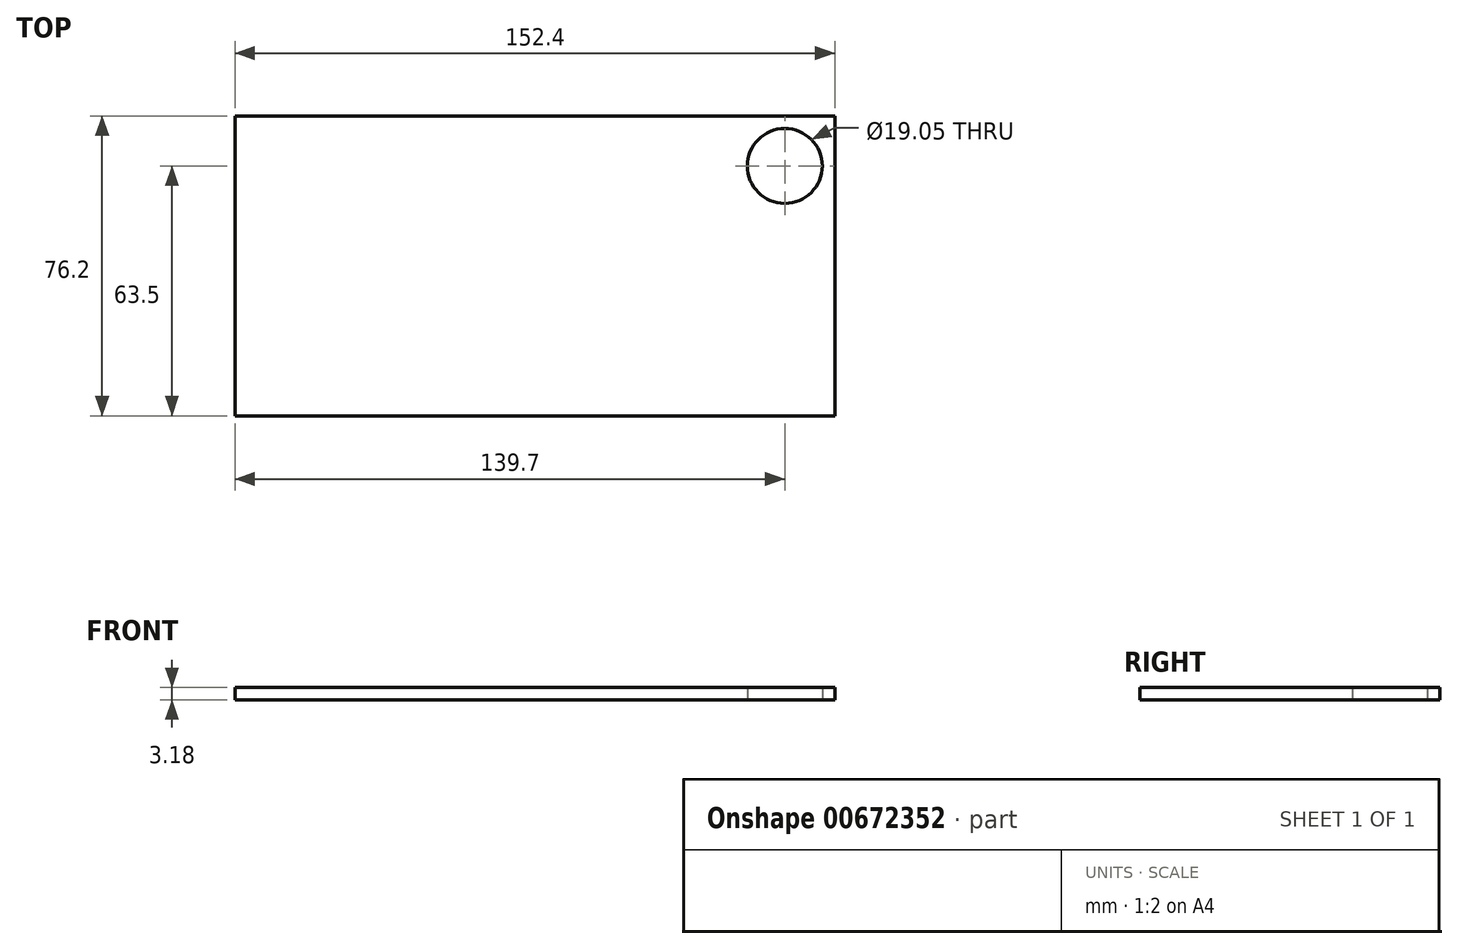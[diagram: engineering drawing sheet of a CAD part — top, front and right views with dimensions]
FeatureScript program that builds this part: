
annotation { "Feature Type Name" : "Feature", "Feature Type Description" : "" }
export const myFeature = defineFeature(function(context is Context, id is Id, definition is map)
    precondition{}
    {
        {
            var Q0;
            Q0=qCreatedBy(makeId("Top.planeOp"),FACE);
            var sketch = newSketch(context, id + "F0", { "sketchPlane" : qUnion([Q0])});
            skLineSegment(sketch, "E0.bottom", {"start": v(-152.4, -76.2) * mm, "end": v(0, -76.2) * mm});
            skLineSegment(sketch, "E0.top", {"start": v(-152.4, 0) * mm, "end": v(0, 0) * mm});
            skLineSegment(sketch, "E0.left", {"start": v(-152.4, -76.2) * mm, "end": v(-152.4, 0) * mm});
            skLineSegment(sketch, "E0.right", {"start": v(0, -76.2) * mm, "end": v(0, 0) * mm});
            skCircle(sketch, "E1", {"center": v(-12.7, -12.7) * mm, "radius": 9.53 * mm});
            skSolve(sketch);
        }
        {
            var Q0;
            Q0=makeQuery(id+"F0.imprint","IMPRINT",FACE,{"disambiguationData":[TD([[makeQuery(id+"F0.imprint","IMPRINT",EDGE,{"derivedFrom":sQuery(id+"F0.wireOp",EDGE,"E0.bottom")}),1.0]])]});
            extrude(context, id + "F1", {"entities" : qUnion([Q0]), "depth" : 3.17 * mm, "offsetDistance" : 25.4 * mm});
        }
    });
